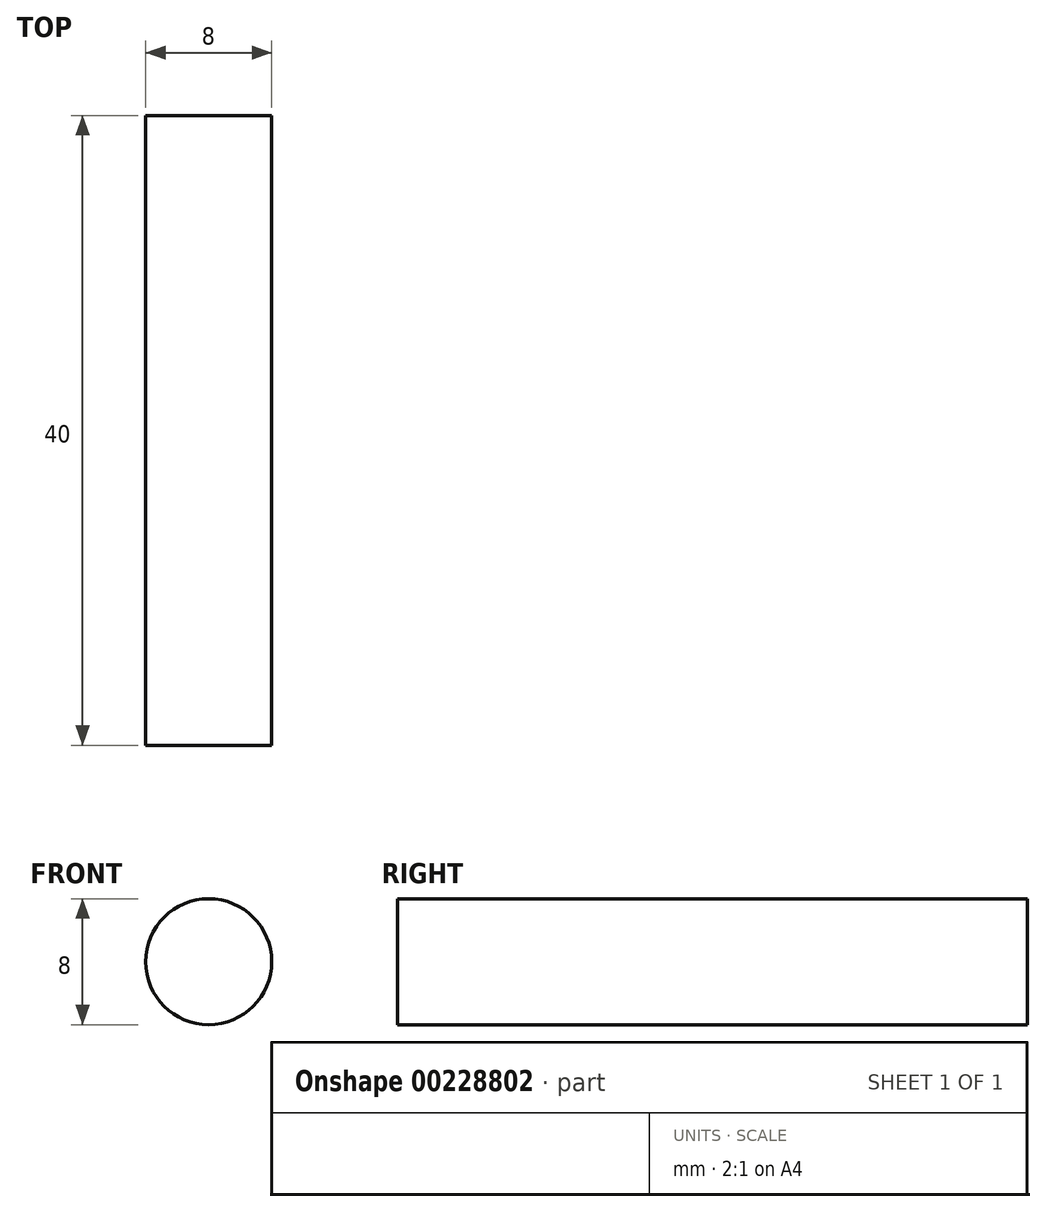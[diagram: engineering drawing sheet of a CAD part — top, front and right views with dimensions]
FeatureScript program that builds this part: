
annotation { "Feature Type Name" : "Feature", "Feature Type Description" : "" }
export const myFeature = defineFeature(function(context is Context, id is Id, definition is map)
    precondition{}
    {
        {
            var Q0;
            Q0=qCreatedBy(makeId("Front.planeOp"),FACE);
            var sketch = newSketch(context, id + "F0", { "sketchPlane" : qUnion([Q0])});
            skCircle(sketch, "E0", {"center": v(0, 0) * mm, "radius": 4 * mm});
            skSolve(sketch);
        }
        {
            var Q0;
            Q0=makeQuery(id+"F0.imprint","IMPRINT",FACE,{"disambiguationData":[TD([[makeQuery(id+"F0.imprint","IMPRINT",EDGE,{"derivedFrom":sQuery(id+"F0.wireOp",EDGE,"E0")}),1.0]])]});
            extrude(context, id + "F1", {"entities" : qUnion([Q0]), "endBound" : BoundingType.SYMMETRIC, "depth" : 40 * mm});
        }
    });
